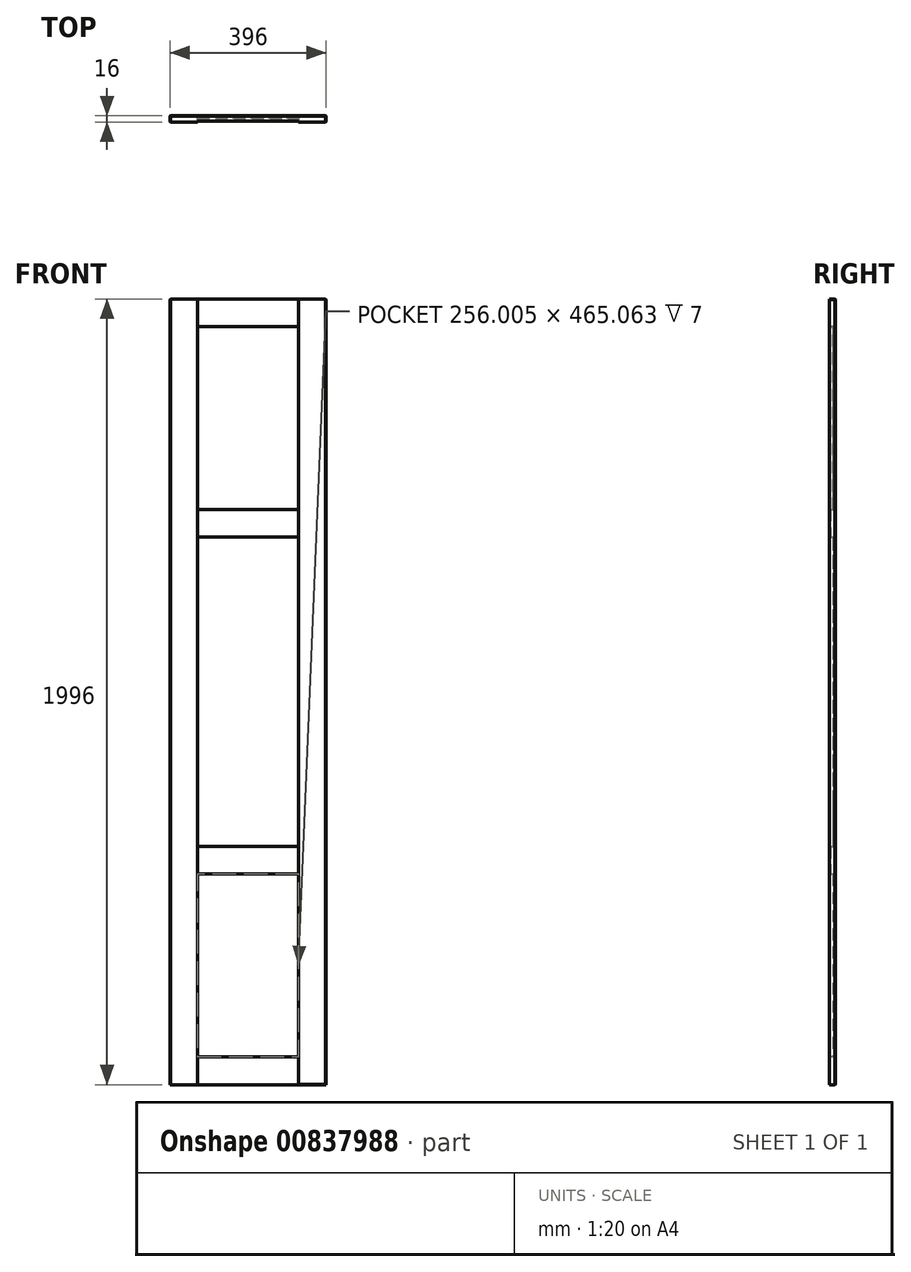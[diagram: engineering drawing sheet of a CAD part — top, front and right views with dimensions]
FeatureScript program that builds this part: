
annotation { "Feature Type Name" : "Feature", "Feature Type Description" : "" }
export const myFeature = defineFeature(function(context is Context, id is Id, definition is map)
    precondition{}
    {
        {
            var Q0;
            Q0=qCreatedBy(makeId("Front.planeOp"),FACE);
            var sketch = newSketch(context, id + "F0", { "sketchPlane" : qUnion([Q0])});
            skLineSegment(sketch, "E0.bottom", {"start": v(0, 0) * mm, "end": v(35.9, 0) * mm});
            skLineSegment(sketch, "E0.top", {"start": v(0, 30.12) * mm, "end": v(35.9, 30.12) * mm});
            skLineSegment(sketch, "E0.left", {"start": v(0, 0) * mm, "end": v(0, 30.12) * mm});
            skLineSegment(sketch, "E0.right", {"start": v(35.9, 0) * mm, "end": v(35.9, 30.12) * mm});
            skSolve(sketch);
        }
        {
            var Q0;
            Q0=makeQuery(id+"F0.imprint","IMPRINT",FACE,{"disambiguationData":[TD([[makeQuery(id+"F0.imprint","IMPRINT",EDGE,{"derivedFrom":sQuery(id+"F0.wireOp",EDGE,"E0.bottom")}),1.0]])]});
            extrude(context, id + "F1", {"entities" : qUnion([Q0]), "depth" : 16 * mm, "offsetDistance" : 25.4 * mm});
        }
        {
            var Q0;
            Q0=makeQuery(id+"F1.opExtrude","SWEPT_FACE",FACE,{"disambiguationData":[OSD([sQuery(id+"F0.wireOp",EDGE,"E0.left")])]});
            extrude(context, id + "F2", {"entities" : qUnion([Q0]), "operationType" : NewBodyOperationType.ADD, "oppositeDirection" : true, "depth" : 196 * mm, "offsetDistance" : 25 * mm});
        }
        {
            var Q0;
            {var subQ0=sQuery(id+"F0.wireOp",EDGE,"E0.bottom");Q0=makeQuery(id+"F2.boolean.opBoolean","MERGE",FACE,{"derivedFrom":[makeQuery(id+"F1.opExtrude","SWEPT_FACE",FACE,{"disambiguationData":[OSD([subQ0])]}),makeQuery(id+"F2.opExtrude","SWEPT_FACE",FACE,{"disambiguationData":[OSD([subQ0,sQuery(id+"F0.wireOp",EDGE,"E0.left")])]})]});}
            extrude(context, id + "F3", {"entities" : qUnion([Q0]), "operationType" : NewBodyOperationType.ADD, "oppositeDirection" : true, "depth" : 796 * mm, "offsetDistance" : 25 * mm});
        }
        {
            var Q0;
            {var subQ0=sQuery(id+"F0.wireOp",EDGE,"E0.left");var subQ1=sQuery(id+"F0.wireOp",EDGE,"E0.bottom");Q0=makeQuery(id+"F3.boolean.opBoolean","MERGE",FACE,{"derivedFrom":[makeQuery(id+"F2.boolean.opBoolean","MERGE",FACE,{"derivedFrom":[makeQuery(id+"F1.opExtrude","CAP_FACE",FACE,{"disambiguationData":[OSD([subQ1,sQuery(id+"F0.wireOp",EDGE,"E0.top"),subQ0,sQuery(id+"F0.wireOp",EDGE,"E0.right")])],"isStart":false}),makeQuery(id+"F2.opExtrude","SWEPT_FACE",FACE,{"disambiguationData":[OSD([subQ0]),TDD([makeQuery(id+"F1.opExtrude","CAP_EDGE",EDGE,{"disambiguationData":[OSD([subQ0])],"isStart":false})])]})]}),makeQuery(id+"F3.opExtrude","SWEPT_FACE",FACE,{"disambiguationData":[OSD([subQ1,subQ0]),TDD([makeQuery(id+"F2.boolean.opBoolean","MERGE",EDGE,{"derivedFrom":[makeQuery(id+"F1.opExtrude","CAP_EDGE",EDGE,{"disambiguationData":[OSD([subQ1])],"isStart":false}),makeQuery(id+"F2.opExtrude","SWEPT_EDGE",EDGE,{"disambiguationData":[OSD([subQ1,subQ0]),TDD([makeQuery(id+"F1.opExtrude","CAP_VERTEX",VERTEX,{"disambiguationData":[OSD([subQ1,subQ0])],"isStart":false})])]})]})])]})]});}
            var sketch = newSketch(context, id + "F4", { "sketchPlane" : qUnion([Q0])});
            skLineSegment(sketch, "E1.bottom", {"start": v(0, 796) * mm, "end": v(42.19, 796) * mm});
            skLineSegment(sketch, "E1.top", {"start": v(0, 751.57) * mm, "end": v(42.19, 751.57) * mm});
            skLineSegment(sketch, "E1.left", {"start": v(0, 796) * mm, "end": v(0, 751.57) * mm});
            skLineSegment(sketch, "E1.right", {"start": v(42.19, 796) * mm, "end": v(42.19, 751.57) * mm});
            skLineSegment(sketch, "E2.bottom", {"start": v(196, 796) * mm, "end": v(153.6, 796) * mm});
            skLineSegment(sketch, "E2.top", {"start": v(196, 746.75) * mm, "end": v(153.6, 746.75) * mm});
            skLineSegment(sketch, "E2.left", {"start": v(196, 796) * mm, "end": v(196, 746.75) * mm});
            skLineSegment(sketch, "E2.right", {"start": v(153.6, 796) * mm, "end": v(153.6, 746.75) * mm});
            skSolve(sketch);
        }
        {
            var Q0;
            Q0=makeQuery(id+"F4.imprint","IMPRINT",FACE,{"disambiguationData":[TD([[makeQuery(id+"F4.imprint","IMPRINT",EDGE,{"derivedFrom":sQuery(id+"F4.wireOp",EDGE,"E1.bottom")}),-1.0]])]});
            var Q1;
            Q1=makeQuery(id+"F4.imprint","IMPRINT",FACE,{"disambiguationData":[TD([[makeQuery(id+"F4.imprint","IMPRINT",EDGE,{"derivedFrom":sQuery(id+"F4.wireOp",EDGE,"E2.bottom")}),-1.0]])]});
            extrude(context, id + "F5", {"entities" : qUnion([Q0, Q1]), "operationType" : NewBodyOperationType.ADD, "depth" : 25 * mm, "offsetDistance" : 25 * mm});
        }
        {
            var Q0;
            {var subQ0=sQuery(id+"F0.wireOp",EDGE,"E0.left");var subQ1=sQuery(id+"F0.wireOp",EDGE,"E0.bottom");Q0=makeQuery(id+"F3.boolean.opBoolean","MERGE",FACE,{"derivedFrom":[makeQuery(id+"F2.boolean.opBoolean","MERGE",FACE,{"derivedFrom":[makeQuery(id+"F1.opExtrude","CAP_FACE",FACE,{"disambiguationData":[OSD([subQ1,sQuery(id+"F0.wireOp",EDGE,"E0.top"),subQ0,sQuery(id+"F0.wireOp",EDGE,"E0.right")])],"isStart":false}),makeQuery(id+"F2.opExtrude","SWEPT_FACE",FACE,{"disambiguationData":[OSD([subQ0]),TDD([makeQuery(id+"F1.opExtrude","CAP_EDGE",EDGE,{"disambiguationData":[OSD([subQ0])],"isStart":false})])]})]}),makeQuery(id+"F3.opExtrude","SWEPT_FACE",FACE,{"disambiguationData":[OSD([subQ1,subQ0]),TDD([makeQuery(id+"F2.boolean.opBoolean","MERGE",EDGE,{"derivedFrom":[makeQuery(id+"F1.opExtrude","CAP_EDGE",EDGE,{"disambiguationData":[OSD([subQ1])],"isStart":false}),makeQuery(id+"F2.opExtrude","SWEPT_EDGE",EDGE,{"disambiguationData":[OSD([subQ1,subQ0]),TDD([makeQuery(id+"F1.opExtrude","CAP_VERTEX",VERTEX,{"disambiguationData":[OSD([subQ1,subQ0])],"isStart":false})])]})]})])]})]});}
            var sketch = newSketch(context, id + "F6", { "sketchPlane" : qUnion([Q0])});
            skLineSegment(sketch, "E3.bottom", {"start": v(196, 0) * mm, "end": v(163.38, 0) * mm});
            skLineSegment(sketch, "E3.top", {"start": v(196, 46.55) * mm, "end": v(163.38, 46.55) * mm});
            skLineSegment(sketch, "E3.left", {"start": v(196, 0) * mm, "end": v(196, 46.55) * mm});
            skLineSegment(sketch, "E3.right", {"start": v(163.38, 0) * mm, "end": v(163.38, 46.55) * mm});
            skLineSegment(sketch, "E4.bottom", {"start": v(0, 0) * mm, "end": v(50.28, 0) * mm});
            skLineSegment(sketch, "E4.top", {"start": v(0, 44.4) * mm, "end": v(50.28, 44.4) * mm});
            skLineSegment(sketch, "E4.left", {"start": v(0, 0) * mm, "end": v(0, 44.4) * mm});
            skLineSegment(sketch, "E4.right", {"start": v(50.28, 0) * mm, "end": v(50.28, 44.4) * mm});
            skSolve(sketch);
        }
        {
            var Q0;
            Q0=makeQuery(id+"F6.imprint","IMPRINT",FACE,{"disambiguationData":[TD([[makeQuery(id+"F6.imprint","IMPRINT",EDGE,{"derivedFrom":sQuery(id+"F6.wireOp",EDGE,"E3.bottom")}),1.0]])]});
            var Q1;
            Q1=makeQuery(id+"F6.imprint","IMPRINT",FACE,{"disambiguationData":[TD([[makeQuery(id+"F6.imprint","IMPRINT",EDGE,{"derivedFrom":sQuery(id+"F6.wireOp",EDGE,"E4.bottom")}),1.0]])]});
            extrude(context, id + "F7", {"entities" : qUnion([Q0, Q1]), "operationType" : NewBodyOperationType.ADD, "depth" : 25 * mm, "offsetDistance" : 25 * mm});
        }
        {
            var Q0;
            Q0=makeQuery(id+"F7.opExtrude","SWEPT_FACE",FACE,{"disambiguationData":[OSD([sQuery(id+"F6.wireOp",EDGE,"E4.right")])]});
            extrude(context, id + "F8", {"entities" : qUnion([Q0]), "operationType" : NewBodyOperationType.ADD, "depth" : 19.72 * mm, "offsetDistance" : 25 * mm});
        }
        {
            var Q0;
            {var subQ0=sQuery(id+"F6.wireOp",EDGE,"E4.top");Q0=makeQuery(id+"F8.boolean.opBoolean","MERGE",FACE,{"derivedFrom":[makeQuery(id+"F7.opExtrude","SWEPT_FACE",FACE,{"disambiguationData":[OSD([subQ0])]}),makeQuery(id+"F8.opExtrude","SWEPT_FACE",FACE,{"disambiguationData":[OSD([subQ0,sQuery(id+"F6.wireOp",EDGE,"E4.right")])]})]});}
            extrude(context, id + "F9", {"entities" : qUnion([Q0]), "operationType" : NewBodyOperationType.ADD, "depth" : 25.6 * mm, "offsetDistance" : 25 * mm});
        }
        {
            var Q0;
            Q0=makeQuery(id+"F7.opExtrude","SWEPT_FACE",FACE,{"disambiguationData":[OSD([sQuery(id+"F6.wireOp",EDGE,"E3.right")])]});
            extrude(context, id + "F10", {"entities" : qUnion([Q0]), "operationType" : NewBodyOperationType.ADD, "depth" : 37.38 * mm, "offsetDistance" : 25 * mm});
        }
        {
            var Q0;
            {var subQ0=sQuery(id+"F6.wireOp",EDGE,"E3.top");Q0=makeQuery(id+"F10.boolean.opBoolean","MERGE",FACE,{"derivedFrom":[makeQuery(id+"F7.opExtrude","SWEPT_FACE",FACE,{"disambiguationData":[OSD([subQ0])]}),makeQuery(id+"F10.opExtrude","SWEPT_FACE",FACE,{"disambiguationData":[OSD([subQ0,sQuery(id+"F6.wireOp",EDGE,"E3.right")])]})]});}
            extrude(context, id + "F11", {"entities" : qUnion([Q0]), "operationType" : NewBodyOperationType.ADD, "depth" : 23.45 * mm, "offsetDistance" : 25 * mm});
        }
        {
            var Q0;
            Q0=makeQuery(id+"F5.opExtrude","SWEPT_FACE",FACE,{"disambiguationData":[OSD([sQuery(id+"F4.wireOp",EDGE,"E1.right")])]});
            extrude(context, id + "F12", {"entities" : qUnion([Q0]), "operationType" : NewBodyOperationType.ADD, "depth" : 27.8 * mm, "offsetDistance" : 25 * mm});
        }
        {
            var Q0;
            {var subQ0=sQuery(id+"F4.wireOp",EDGE,"E1.top");Q0=makeQuery(id+"F12.boolean.opBoolean","MERGE",FACE,{"derivedFrom":[makeQuery(id+"F5.opExtrude","SWEPT_FACE",FACE,{"disambiguationData":[OSD([subQ0])]}),makeQuery(id+"F12.opExtrude","SWEPT_FACE",FACE,{"disambiguationData":[OSD([subQ0,sQuery(id+"F4.wireOp",EDGE,"E1.right")])]})]});}
            extrude(context, id + "F13", {"entities" : qUnion([Q0]), "operationType" : NewBodyOperationType.ADD, "depth" : 25.57 * mm, "offsetDistance" : 25 * mm});
        }
        {
            var Q0;
            Q0=makeQuery(id+"F5.opExtrude","SWEPT_FACE",FACE,{"disambiguationData":[OSD([sQuery(id+"F4.wireOp",EDGE,"E2.top")])]});
            extrude(context, id + "F14", {"entities" : qUnion([Q0]), "operationType" : NewBodyOperationType.ADD, "depth" : 20.75 * mm, "offsetDistance" : 25 * mm});
        }
        {
            var Q0;
            {var subQ0=sQuery(id+"F4.wireOp",EDGE,"E2.right");Q0=makeQuery(id+"F14.boolean.opBoolean","MERGE",FACE,{"derivedFrom":[makeQuery(id+"F5.opExtrude","SWEPT_FACE",FACE,{"disambiguationData":[OSD([subQ0])]}),makeQuery(id+"F14.opExtrude","SWEPT_FACE",FACE,{"disambiguationData":[OSD([sQuery(id+"F4.wireOp",EDGE,"E2.top"),subQ0])]})]});}
            extrude(context, id + "F15", {"entities" : qUnion([Q0]), "operationType" : NewBodyOperationType.ADD, "depth" : 27.6 * mm, "offsetDistance" : 25 * mm});
        }
        {
            var Q0;
            {var subQ0=sQuery(id+"F0.wireOp",EDGE,"E0.left");var subQ1=sQuery(id+"F0.wireOp",EDGE,"E0.bottom");Q0=makeQuery(id+"F3.boolean.opBoolean","MERGE",FACE,{"derivedFrom":[makeQuery(id+"F2.boolean.opBoolean","MERGE",FACE,{"derivedFrom":[makeQuery(id+"F1.opExtrude","CAP_FACE",FACE,{"disambiguationData":[OSD([subQ1,sQuery(id+"F0.wireOp",EDGE,"E0.top"),subQ0,sQuery(id+"F0.wireOp",EDGE,"E0.right")])],"isStart":false}),makeQuery(id+"F2.opExtrude","SWEPT_FACE",FACE,{"disambiguationData":[OSD([subQ0]),TDD([makeQuery(id+"F1.opExtrude","CAP_EDGE",EDGE,{"disambiguationData":[OSD([subQ0])],"isStart":false})])]})]}),makeQuery(id+"F3.opExtrude","SWEPT_FACE",FACE,{"disambiguationData":[OSD([subQ1,subQ0]),TDD([makeQuery(id+"F2.boolean.opBoolean","MERGE",EDGE,{"derivedFrom":[makeQuery(id+"F1.opExtrude","CAP_EDGE",EDGE,{"disambiguationData":[OSD([subQ1])],"isStart":false}),makeQuery(id+"F2.opExtrude","SWEPT_EDGE",EDGE,{"disambiguationData":[OSD([subQ1,subQ0]),TDD([makeQuery(id+"F1.opExtrude","CAP_VERTEX",VERTEX,{"disambiguationData":[OSD([subQ1,subQ0])],"isStart":false})])]})]})])]})]});}
            var sketch = newSketch(context, id + "F16", { "sketchPlane" : qUnion([Q0])});
            skLineSegment(sketch, "E5.bottom", {"start": v(70, 726) * mm, "end": v(126, 726) * mm});
            skLineSegment(sketch, "E5.top", {"start": v(70, 70) * mm, "end": v(126, 70) * mm});
            skLineSegment(sketch, "E5.left", {"start": v(70, 726) * mm, "end": v(70, 70) * mm});
            skLineSegment(sketch, "E5.right", {"start": v(126, 726) * mm, "end": v(126, 70) * mm});
            skSolve(sketch);
        }
        {
            var Q0;
            Q0=makeQuery(id+"F16.imprint","IMPRINT",FACE,{"disambiguationData":[TD([[makeQuery(id+"F16.imprint","IMPRINT",EDGE,{"derivedFrom":sQuery(id+"F16.wireOp",EDGE,"E5.top")}),1.0]])]});
            extrude(context, id + "F17", {"entities" : qUnion([Q0]), "operationType" : NewBodyOperationType.REMOVE, "oppositeDirection" : true, "depth" : 10 * mm, "offsetDistance" : 25 * mm});
        }
        {
            var Q0;
            {var subQ2=sQuery(id+"F0.wireOp",EDGE,"E0.left");var subQ3=sQuery(id+"F0.wireOp",EDGE,"E0.bottom");var subQ4=makeQuery(id+"F1.opExtrude","CAP_FACE",FACE,{"disambiguationData":[OSD([subQ3,sQuery(id+"F0.wireOp",EDGE,"E0.top"),subQ2,sQuery(id+"F0.wireOp",EDGE,"E0.right")])],"isStart":false});var subQ7=makeQuery(id+"F3.opExtrude","SWEPT_FACE",FACE,{"disambiguationData":[OSD([subQ3,subQ2]),TDD([makeQuery(id+"F2.boolean.opBoolean","MERGE",EDGE,{"derivedFrom":[makeQuery(id+"F1.opExtrude","CAP_EDGE",EDGE,{"disambiguationData":[OSD([subQ3])],"isStart":false}),makeQuery(id+"F2.opExtrude","SWEPT_EDGE",EDGE,{"disambiguationData":[OSD([subQ3,subQ2]),TDD([makeQuery(id+"F1.opExtrude","CAP_VERTEX",VERTEX,{"disambiguationData":[OSD([subQ3,subQ2])],"isStart":false})])]})]})])]});var subQ8=makeQuery(id+"F2.opExtrude","SWEPT_FACE",FACE,{"disambiguationData":[OSD([subQ2]),TDD([makeQuery(id+"F1.opExtrude","CAP_EDGE",EDGE,{"disambiguationData":[OSD([subQ2])],"isStart":false})])]});Q0=makeQuery(id+"F17.boolean.opBoolean","SPLIT",FACE,{"disambiguationData":[TD([makeQuery(id+"F1.opExtrude","SWEPT_FACE",FACE,{"disambiguationData":[OSD([subQ3])]})])],"derivedFrom":makeQuery(id+"F3.boolean.opBoolean","MERGE",FACE,{"derivedFrom":[makeQuery(id+"F2.boolean.opBoolean","MERGE",FACE,{"derivedFrom":[subQ4,subQ8]}),subQ7]})});}
            var Q1;
            {var subQ2=sQuery(id+"F4.wireOp",EDGE,"E1.bottom");var subQ3=sQuery(id+"F0.wireOp",EDGE,"E0.left");var subQ4=sQuery(id+"F0.wireOp",EDGE,"E0.bottom");var subQ6=makeQuery(id+"F1.opExtrude","CAP_FACE",FACE,{"disambiguationData":[OSD([subQ4,sQuery(id+"F0.wireOp",EDGE,"E0.top"),subQ3,sQuery(id+"F0.wireOp",EDGE,"E0.right")])],"isStart":false});var subQ7=makeQuery(id+"F2.opExtrude","SWEPT_FACE",FACE,{"disambiguationData":[OSD([subQ3]),TDD([makeQuery(id+"F1.opExtrude","CAP_EDGE",EDGE,{"disambiguationData":[OSD([subQ3])],"isStart":false})])]});var subQ8=makeQuery(id+"F3.opExtrude","SWEPT_FACE",FACE,{"disambiguationData":[OSD([subQ4,subQ3]),TDD([makeQuery(id+"F2.boolean.opBoolean","MERGE",EDGE,{"derivedFrom":[makeQuery(id+"F1.opExtrude","CAP_EDGE",EDGE,{"disambiguationData":[OSD([subQ4])],"isStart":false}),makeQuery(id+"F2.opExtrude","SWEPT_EDGE",EDGE,{"disambiguationData":[OSD([subQ4,subQ3]),TDD([makeQuery(id+"F1.opExtrude","CAP_VERTEX",VERTEX,{"disambiguationData":[OSD([subQ4,subQ3])],"isStart":false})])]})]})])]});Q1=makeQuery(id+"F17.boolean.opBoolean","SPLIT",FACE,{"disambiguationData":[TD([makeQuery(id+"F5.opExtrude","SWEPT_FACE",FACE,{"disambiguationData":[OSD([subQ2])]})])],"derivedFrom":makeQuery(id+"F3.boolean.opBoolean","MERGE",FACE,{"derivedFrom":[makeQuery(id+"F2.boolean.opBoolean","MERGE",FACE,{"derivedFrom":[subQ6,subQ7]}),subQ8]})});}
            extrude(context, id + "F18", {"entities" : qUnion([Q0, Q1]), "operationType" : NewBodyOperationType.REMOVE, "oppositeDirection" : true, "depth" : 2 * mm, "offsetDistance" : 25 * mm});
        }
        {
            var Q0;
            {var subQ0=sQuery(id+"F4.wireOp",EDGE,"E1.right");var subQ1=sQuery(id+"F4.wireOp",EDGE,"E1.top");Q0=makeQuery(id+"F13.boolean.opBoolean","MERGE",FACE,{"derivedFrom":[makeQuery(id+"F12.boolean.opBoolean","MERGE",FACE,{"derivedFrom":[makeQuery(id+"F5.opExtrude","CAP_FACE",FACE,{"disambiguationData":[OSD([sQuery(id+"F4.wireOp",EDGE,"E1.bottom"),subQ1,sQuery(id+"F4.wireOp",EDGE,"E1.left"),subQ0])],"isStart":false}),makeQuery(id+"F12.opExtrude","SWEPT_FACE",FACE,{"disambiguationData":[OSD([subQ0]),TDD([makeQuery(id+"F5.opExtrude","CAP_EDGE",EDGE,{"disambiguationData":[OSD([subQ0])],"isStart":false})])]})]}),makeQuery(id+"F13.opExtrude","SWEPT_FACE",FACE,{"disambiguationData":[OSD([subQ1,subQ0]),TDD([makeQuery(id+"F12.boolean.opBoolean","MERGE",EDGE,{"derivedFrom":[makeQuery(id+"F5.opExtrude","CAP_EDGE",EDGE,{"disambiguationData":[OSD([subQ1])],"isStart":false}),makeQuery(id+"F12.opExtrude","SWEPT_EDGE",EDGE,{"disambiguationData":[OSD([subQ1,subQ0]),TDD([makeQuery(id+"F5.opExtrude","CAP_VERTEX",VERTEX,{"disambiguationData":[OSD([subQ1,subQ0])],"isStart":false})])]})]})])]})]});}
            var Q1;
            {var subQ0=sQuery(id+"F4.wireOp",EDGE,"E2.right");var subQ1=sQuery(id+"F4.wireOp",EDGE,"E2.top");Q1=makeQuery(id+"F15.boolean.opBoolean","MERGE",FACE,{"derivedFrom":[makeQuery(id+"F14.boolean.opBoolean","MERGE",FACE,{"derivedFrom":[makeQuery(id+"F5.opExtrude","CAP_FACE",FACE,{"disambiguationData":[OSD([sQuery(id+"F4.wireOp",EDGE,"E2.bottom"),subQ1,sQuery(id+"F4.wireOp",EDGE,"E2.left"),subQ0])],"isStart":false}),makeQuery(id+"F14.opExtrude","SWEPT_FACE",FACE,{"disambiguationData":[OSD([subQ1]),TDD([makeQuery(id+"F5.opExtrude","CAP_EDGE",EDGE,{"disambiguationData":[OSD([subQ1])],"isStart":false})])]})]}),makeQuery(id+"F15.opExtrude","SWEPT_FACE",FACE,{"disambiguationData":[OSD([subQ1,subQ0]),TDD([makeQuery(id+"F14.boolean.opBoolean","MERGE",EDGE,{"derivedFrom":[makeQuery(id+"F5.opExtrude","CAP_EDGE",EDGE,{"disambiguationData":[OSD([subQ0])],"isStart":false}),makeQuery(id+"F14.opExtrude","SWEPT_EDGE",EDGE,{"disambiguationData":[OSD([subQ1,subQ0]),TDD([makeQuery(id+"F5.opExtrude","CAP_VERTEX",VERTEX,{"disambiguationData":[OSD([subQ1,subQ0])],"isStart":false})])]})]})])]})]});}
            var Q2;
            {var subQ0=sQuery(id+"F6.wireOp",EDGE,"E4.right");var subQ1=sQuery(id+"F6.wireOp",EDGE,"E4.top");Q2=makeQuery(id+"F9.boolean.opBoolean","MERGE",FACE,{"derivedFrom":[makeQuery(id+"F8.boolean.opBoolean","MERGE",FACE,{"derivedFrom":[makeQuery(id+"F7.opExtrude","CAP_FACE",FACE,{"disambiguationData":[OSD([sQuery(id+"F6.wireOp",EDGE,"E4.bottom"),subQ1,sQuery(id+"F6.wireOp",EDGE,"E4.left"),subQ0])],"isStart":false}),makeQuery(id+"F8.opExtrude","SWEPT_FACE",FACE,{"disambiguationData":[OSD([subQ0]),TDD([makeQuery(id+"F7.opExtrude","CAP_EDGE",EDGE,{"disambiguationData":[OSD([subQ0])],"isStart":false})])]})]}),makeQuery(id+"F9.opExtrude","SWEPT_FACE",FACE,{"disambiguationData":[OSD([subQ1,subQ0]),TDD([makeQuery(id+"F8.boolean.opBoolean","MERGE",EDGE,{"derivedFrom":[makeQuery(id+"F7.opExtrude","CAP_EDGE",EDGE,{"disambiguationData":[OSD([subQ1])],"isStart":false}),makeQuery(id+"F8.opExtrude","SWEPT_EDGE",EDGE,{"disambiguationData":[OSD([subQ1,subQ0]),TDD([makeQuery(id+"F7.opExtrude","CAP_VERTEX",VERTEX,{"disambiguationData":[OSD([subQ1,subQ0])],"isStart":false})])]})]})])]})]});}
            var Q3;
            {var subQ0=sQuery(id+"F6.wireOp",EDGE,"E3.right");var subQ1=sQuery(id+"F6.wireOp",EDGE,"E3.top");Q3=makeQuery(id+"F11.boolean.opBoolean","MERGE",FACE,{"derivedFrom":[makeQuery(id+"F10.boolean.opBoolean","MERGE",FACE,{"derivedFrom":[makeQuery(id+"F7.opExtrude","CAP_FACE",FACE,{"disambiguationData":[OSD([sQuery(id+"F6.wireOp",EDGE,"E3.bottom"),subQ1,sQuery(id+"F6.wireOp",EDGE,"E3.left"),subQ0])],"isStart":false}),makeQuery(id+"F10.opExtrude","SWEPT_FACE",FACE,{"disambiguationData":[OSD([subQ0]),TDD([makeQuery(id+"F7.opExtrude","CAP_EDGE",EDGE,{"disambiguationData":[OSD([subQ0])],"isStart":false})])]})]}),makeQuery(id+"F11.opExtrude","SWEPT_FACE",FACE,{"disambiguationData":[OSD([subQ1,subQ0]),TDD([makeQuery(id+"F10.boolean.opBoolean","MERGE",EDGE,{"derivedFrom":[makeQuery(id+"F7.opExtrude","CAP_EDGE",EDGE,{"disambiguationData":[OSD([subQ1])],"isStart":false}),makeQuery(id+"F10.opExtrude","SWEPT_EDGE",EDGE,{"disambiguationData":[OSD([subQ1,subQ0]),TDD([makeQuery(id+"F7.opExtrude","CAP_VERTEX",VERTEX,{"disambiguationData":[OSD([subQ1,subQ0])],"isStart":false})])]})]})])]})]});}
            extrude(context, id + "F19", {"entities" : qUnion([Q0, Q1, Q2, Q3]), "operationType" : NewBodyOperationType.REMOVE, "oppositeDirection" : true, "depth" : 25 * mm, "offsetDistance" : 25 * mm});
        }
        {
            var Q0;
            {var subQ0=sQuery(id+"F4.wireOp",EDGE,"E2.left");var subQ1=sQuery(id+"F0.wireOp",EDGE,"E0.left");var subQ2=sQuery(id+"F0.wireOp",EDGE,"E0.bottom");var subQ3=sQuery(id+"F6.wireOp",EDGE,"E3.left");Q0=makeQuery(id+"F14.boolean.opBoolean","MERGE",FACE,{"derivedFrom":[makeQuery(id+"F11.boolean.opBoolean","MERGE",FACE,{"derivedFrom":[makeQuery(id+"F7.boolean.opBoolean","MERGE",FACE,{"derivedFrom":[makeQuery(id+"F5.boolean.opBoolean","MERGE",FACE,{"derivedFrom":[makeQuery(id+"F3.boolean.opBoolean","MERGE",FACE,{"derivedFrom":[makeQuery(id+"F2.opExtrude","CAP_FACE",FACE,{"disambiguationData":[OSD([subQ1])],"isStart":false}),makeQuery(id+"F3.opExtrude","SWEPT_FACE",FACE,{"disambiguationData":[OSD([subQ2,subQ1]),TDD([makeQuery(id+"F2.opExtrude","CAP_EDGE",EDGE,{"disambiguationData":[OSD([subQ2,subQ1])],"isStart":false})])]})]}),makeQuery(id+"F5.opExtrude","SWEPT_FACE",FACE,{"disambiguationData":[OSD([subQ0])]})]}),makeQuery(id+"F7.opExtrude","SWEPT_FACE",FACE,{"disambiguationData":[OSD([subQ3])]})]}),makeQuery(id+"F11.opExtrude","SWEPT_FACE",FACE,{"disambiguationData":[OSD([subQ2,subQ1,sQuery(id+"F6.wireOp",EDGE,"E3.top"),subQ3])]})]}),makeQuery(id+"F14.opExtrude","SWEPT_FACE",FACE,{"disambiguationData":[OSD([subQ2,subQ1,sQuery(id+"F4.wireOp",EDGE,"E2.top"),subQ0])]})]});}
            extrude(context, id + "F20", {"entities" : qUnion([Q0]), "operationType" : NewBodyOperationType.ADD, "depth" : 200 * mm, "offsetDistance" : 25 * mm});
        }
        {
            var Q0;
            {var subQ0=sQuery(id+"F4.wireOp",EDGE,"E2.right");var subQ1=sQuery(id+"F4.wireOp",EDGE,"E2.top");Q0=makeQuery(id+"F18.boolean.opBoolean","MERGE",FACE,{"derivedFrom":[makeQuery(id+"F15.opExtrude","CAP_FACE",FACE,{"disambiguationData":[OSD([subQ1,subQ0])],"isStart":false}),makeQuery(id+"F18.opExtrude","SWEPT_FACE",FACE,{"disambiguationData":[OSD([subQ1,subQ0])]})]});}
            var Q1;
            {var subQ0=sQuery(id+"F6.wireOp",EDGE,"E3.right");var subQ1=sQuery(id+"F6.wireOp",EDGE,"E3.top");Q1=makeQuery(id+"F18.boolean.opBoolean","MERGE",FACE,{"derivedFrom":[makeQuery(id+"F11.boolean.opBoolean","MERGE",FACE,{"derivedFrom":[makeQuery(id+"F10.opExtrude","CAP_FACE",FACE,{"disambiguationData":[OSD([subQ0])],"isStart":false}),makeQuery(id+"F11.opExtrude","SWEPT_FACE",FACE,{"disambiguationData":[OSD([subQ1,subQ0]),TDD([makeQuery(id+"F10.opExtrude","CAP_EDGE",EDGE,{"disambiguationData":[OSD([subQ1,subQ0])],"isStart":false})])]})]}),makeQuery(id+"F17.boolean.opBoolean","COPY",FACE,{"derivedFrom":makeQuery(id+"F17.opExtrude","SWEPT_FACE",FACE,{"disambiguationData":[OSD([sQuery(id+"F16.wireOp",EDGE,"E5.right")])]})}),makeQuery(id+"F18.opExtrude","SWEPT_FACE",FACE,{"disambiguationData":[OSD([subQ1,subQ0])]})]});}
            extrude(context, id + "F21", {"entities" : qUnion([Q0, Q1]), "operationType" : NewBodyOperationType.REMOVE, "oppositeDirection" : true, "depth" : 200 * mm, "offsetDistance" : 25 * mm});
        }
        {
            var Q0;
            {var subQ0=sQuery(id+"F4.wireOp",EDGE,"E2.bottom");var subQ1=sQuery(id+"F0.wireOp",EDGE,"E0.left");var subQ2=sQuery(id+"F0.wireOp",EDGE,"E0.bottom");var subQ3=sQuery(id+"F4.wireOp",EDGE,"E1.bottom");Q0=makeQuery(id+"F20.boolean.opBoolean","MERGE",FACE,{"derivedFrom":[makeQuery(id+"F15.boolean.opBoolean","MERGE",FACE,{"derivedFrom":[makeQuery(id+"F12.boolean.opBoolean","MERGE",FACE,{"derivedFrom":[makeQuery(id+"F5.boolean.opBoolean","MERGE",FACE,{"derivedFrom":[makeQuery(id+"F3.opExtrude","CAP_FACE",FACE,{"disambiguationData":[OSD([subQ2,subQ1])],"isStart":false}),makeQuery(id+"F5.opExtrude","SWEPT_FACE",FACE,{"disambiguationData":[OSD([subQ3])]}),makeQuery(id+"F5.opExtrude","SWEPT_FACE",FACE,{"disambiguationData":[OSD([subQ0])]})]}),makeQuery(id+"F12.opExtrude","SWEPT_FACE",FACE,{"disambiguationData":[OSD([subQ2,subQ1,subQ3,sQuery(id+"F4.wireOp",EDGE,"E1.right")])]})]}),makeQuery(id+"F15.opExtrude","SWEPT_FACE",FACE,{"disambiguationData":[OSD([subQ2,subQ1,subQ0,sQuery(id+"F4.wireOp",EDGE,"E2.right")])]})]}),makeQuery(id+"F20.opExtrude","SWEPT_FACE",FACE,{"disambiguationData":[OSD([subQ2,subQ1,subQ0,sQuery(id+"F4.wireOp",EDGE,"E2.left")])]})]});}
            extrude(context, id + "F22", {"entities" : qUnion([Q0]), "operationType" : NewBodyOperationType.ADD, "depth" : 200 * mm, "offsetDistance" : 25 * mm});
        }
        {
            var Q0;
            Q0=makeQuery(id+"F17.boolean.opBoolean","COPY",FACE,{"derivedFrom":makeQuery(id+"F17.opExtrude","SWEPT_FACE",FACE,{"disambiguationData":[OSD([sQuery(id+"F16.wireOp",EDGE,"E5.bottom")])]})});
            var Q1;
            {var subQ0=sQuery(id+"F16.wireOp",EDGE,"E5.right");var subQ1=sQuery(id+"F16.wireOp",EDGE,"E5.bottom");var subQ2=sQuery(id+"F4.wireOp",EDGE,"E2.right");var subQ3=sQuery(id+"F4.wireOp",EDGE,"E2.top");var subQ4=makeQuery(id+"F17.boolean.opBoolean","COPY",EDGE,{"derivedFrom":makeQuery(id+"F17.opExtrude","SWEPT_EDGE",EDGE,{"disambiguationData":[OSD([subQ3,subQ2,subQ1,subQ0])]})});Q1=makeQuery(id+"F21.boolean.opBoolean","COPY",FACE,{"derivedFrom":makeQuery(id+"F21.opExtrude","SWEPT_FACE",FACE,{"disambiguationData":[OSD([subQ3,subQ2,subQ1,subQ0]),TDD([makeQuery(id+"F18.boolean.opBoolean","MERGE",EDGE,{"derivedFrom":[subQ4,makeQuery(id+"F18.opExtrude","SWEPT_EDGE",EDGE,{"disambiguationData":[OSD([subQ3,subQ2,subQ1,subQ0])]})]}),makeQuery(id+"F18.boolean.opBoolean","SPLIT",EDGE,{"derivedFrom":subQ4})])]})});}
            extrude(context, id + "F23", {"entities" : qUnion([Q0, Q1]), "operationType" : NewBodyOperationType.REMOVE, "oppositeDirection" : true, "depth" : 200 * mm, "offsetDistance" : 25 * mm});
        }
        {
            var Q0;
            Q0=makeQuery(id+"F22.opExtrude","CAP_FACE",FACE,{"disambiguationData":[OSD([sQuery(id+"F0.wireOp",EDGE,"E0.bottom"),sQuery(id+"F0.wireOp",EDGE,"E0.left"),sQuery(id+"F4.wireOp",EDGE,"E1.bottom"),sQuery(id+"F4.wireOp",EDGE,"E1.right"),sQuery(id+"F4.wireOp",EDGE,"E2.bottom"),sQuery(id+"F4.wireOp",EDGE,"E2.left"),sQuery(id+"F4.wireOp",EDGE,"E2.right")])],"isStart":false});
            extrude(context, id + "F24", {"entities" : qUnion([Q0]), "operationType" : NewBodyOperationType.ADD, "depth" : 1000 * mm, "offsetDistance" : 25 * mm});
        }
        {
            var Q0;
            Q0=makeQuery(id+"F23.boolean.opBoolean","COPY",FACE,{"derivedFrom":makeQuery(id+"F23.opExtrude","CAP_FACE",FACE,{"disambiguationData":[OSD([sQuery(id+"F16.wireOp",EDGE,"E5.bottom")])],"isStart":false})});
            var Q1;
            Q1=makeQuery(id+"F23.boolean.opBoolean","COPY",FACE,{"derivedFrom":makeQuery(id+"F23.opExtrude","CAP_FACE",FACE,{"disambiguationData":[OSD([sQuery(id+"F4.wireOp",EDGE,"E2.top"),sQuery(id+"F4.wireOp",EDGE,"E2.right"),sQuery(id+"F16.wireOp",EDGE,"E5.bottom"),sQuery(id+"F16.wireOp",EDGE,"E5.right")])],"isStart":false})});
            extrude(context, id + "F25", {"entities" : qUnion([Q0, Q1]), "operationType" : NewBodyOperationType.REMOVE, "oppositeDirection" : true, "depth" : 1000 * mm, "offsetDistance" : 25 * mm});
        }
        {
            var Q0;
            {var subQ0=sQuery(id+"F16.wireOp",EDGE,"E5.left");var subQ1=sQuery(id+"F16.wireOp",EDGE,"E5.bottom");var subQ2=sQuery(id+"F4.wireOp",EDGE,"E1.right");var subQ3=sQuery(id+"F4.wireOp",EDGE,"E1.top");var subQ4=sQuery(id+"F4.wireOp",EDGE,"E1.bottom");var subQ5=sQuery(id+"F0.wireOp",EDGE,"E0.left");var subQ6=sQuery(id+"F0.wireOp",EDGE,"E0.bottom");var subQ7=makeQuery(id+"F18.boolean.opBoolean","MERGE",EDGE,{"derivedFrom":[makeQuery(id+"F12.opExtrude","CAP_EDGE",EDGE,{"disambiguationData":[OSD([subQ6,subQ5,subQ4,subQ2])],"isStart":false}),makeQuery(id+"F18.opExtrude","SWEPT_EDGE",EDGE,{"disambiguationData":[OSD([subQ6,subQ5,subQ4,subQ2])]})]});Q0=makeQuery(id+"F25.boolean.opBoolean","MERGE",FACE,{"derivedFrom":[makeQuery(id+"F24.boolean.opBoolean","MERGE",FACE,{"derivedFrom":[makeQuery(id+"F23.boolean.opBoolean","MERGE",FACE,{"derivedFrom":[makeQuery(id+"F22.boolean.opBoolean","MERGE",FACE,{"derivedFrom":[makeQuery(id+"F18.boolean.opBoolean","MERGE",FACE,{"derivedFrom":[makeQuery(id+"F13.boolean.opBoolean","MERGE",FACE,{"derivedFrom":[makeQuery(id+"F12.opExtrude","CAP_FACE",FACE,{"disambiguationData":[OSD([subQ2])],"isStart":false}),makeQuery(id+"F13.opExtrude","SWEPT_FACE",FACE,{"disambiguationData":[OSD([subQ3,subQ2]),TDD([makeQuery(id+"F12.opExtrude","CAP_EDGE",EDGE,{"disambiguationData":[OSD([subQ3,subQ2])],"isStart":false})])]})]}),makeQuery(id+"F17.boolean.opBoolean","COPY",FACE,{"derivedFrom":makeQuery(id+"F17.opExtrude","SWEPT_FACE",FACE,{"disambiguationData":[OSD([subQ0])]})}),makeQuery(id+"F18.opExtrude","SWEPT_FACE",FACE,{"disambiguationData":[OSD([subQ3,subQ2])]})]}),makeQuery(id+"F22.opExtrude","SWEPT_FACE",FACE,{"disambiguationData":[OSD([subQ6,subQ5,subQ4,subQ2]),TDD([subQ7])]})]}),makeQuery(id+"F23.opExtrude","SWEPT_FACE",FACE,{"disambiguationData":[OSD([subQ3,subQ2,subQ1,subQ0])]})]}),makeQuery(id+"F24.opExtrude","SWEPT_FACE",FACE,{"disambiguationData":[OSD([subQ6,subQ5,subQ4,subQ2]),TDD([makeQuery(id+"F22.opExtrude","CAP_EDGE",EDGE,{"disambiguationData":[OSD([subQ6,subQ5,subQ4,subQ2]),TDD([subQ7])],"isStart":false})])]})]}),makeQuery(id+"F25.opExtrude","SWEPT_FACE",FACE,{"disambiguationData":[OSD([subQ3,subQ2,subQ1,subQ0])]})]});}
            var sketch = newSketch(context, id + "F26", { "sketchPlane" : qUnion([Q0])});
            skLineSegment(sketch, "E6.bottom", {"start": v(-16, 70) * mm, "end": v(-6, 70) * mm});
            skLineSegment(sketch, "E6.top", {"start": v(-16, 149.51) * mm, "end": v(-6, 149.51) * mm});
            skLineSegment(sketch, "E6.left", {"start": v(-16, 70) * mm, "end": v(-16, 149.51) * mm});
            skLineSegment(sketch, "E6.right", {"start": v(-6, 70) * mm, "end": v(-6, 149.51) * mm});
            skSolve(sketch);
        }
        {
            var Q0;
            Q0=makeQuery(id+"F26.imprint","IMPRINT",FACE,{"disambiguationData":[TD([[makeQuery(id+"F26.imprint","IMPRINT",EDGE,{"derivedFrom":sQuery(id+"F26.wireOp",EDGE,"E6.top")}),-1.0]])]});
            extrude(context, id + "F27", {"entities" : qUnion([Q0]), "operationType" : NewBodyOperationType.ADD, "depth" : 25 * mm, "offsetDistance" : 25 * mm});
        }
        {
            var Q0;
            Q0=makeQuery(id+"F27.opExtrude","SWEPT_FACE",FACE,{"disambiguationData":[OSD([sQuery(id+"F26.wireOp",EDGE,"E6.top")])]});
            extrude(context, id + "F28", {"entities" : qUnion([Q0]), "operationType" : NewBodyOperationType.ADD, "depth" : 370.48 * mm, "offsetDistance" : 25 * mm});
        }
        {
            var Q0;
            {var subQ0=sQuery(id+"F16.wireOp",EDGE,"E5.right");var subQ1=sQuery(id+"F16.wireOp",EDGE,"E5.bottom");var subQ2=sQuery(id+"F4.wireOp",EDGE,"E2.right");var subQ3=sQuery(id+"F4.wireOp",EDGE,"E2.top");var subQ4=makeQuery(id+"F21.boolean.opBoolean","COPY",EDGE,{"derivedFrom":makeQuery(id+"F21.opExtrude","SWEPT_EDGE",EDGE,{"disambiguationData":[OSD([subQ3,subQ2,subQ1,subQ0]),TDD([makeQuery(id+"F17.boolean.opBoolean","COPY",VERTEX,{"derivedFrom":makeQuery(id+"F17.opExtrude","CAP_VERTEX",VERTEX,{"disambiguationData":[OSD([subQ3,subQ2,subQ1,subQ0])],"isStart":false})})])]})});var subQ5=makeQuery(id+"F17.boolean.opBoolean","COPY",EDGE,{"derivedFrom":makeQuery(id+"F17.opExtrude","CAP_EDGE",EDGE,{"disambiguationData":[OSD([subQ1])],"isStart":false})});Q0=makeQuery(id+"F25.boolean.opBoolean","MERGE",FACE,{"derivedFrom":[makeQuery(id+"F23.boolean.opBoolean","MERGE",FACE,{"derivedFrom":[makeQuery(id+"F21.boolean.opBoolean","MERGE",FACE,{"derivedFrom":[makeQuery(id+"F17.boolean.opBoolean","COPY",FACE,{"derivedFrom":makeQuery(id+"F17.opExtrude","CAP_FACE",FACE,{"disambiguationData":[OSD([subQ1,sQuery(id+"F16.wireOp",EDGE,"E5.top"),sQuery(id+"F16.wireOp",EDGE,"E5.left"),subQ0])],"isStart":false})}),makeQuery(id+"F21.opExtrude","SWEPT_FACE",FACE,{"disambiguationData":[OSD([subQ0])]})]}),makeQuery(id+"F23.opExtrude","SWEPT_FACE",FACE,{"disambiguationData":[OSD([subQ1]),TDD([subQ5])]}),makeQuery(id+"F23.opExtrude","SWEPT_FACE",FACE,{"disambiguationData":[OSD([subQ3,subQ2,subQ1,subQ0]),TDD([subQ4])]})]}),makeQuery(id+"F25.opExtrude","SWEPT_FACE",FACE,{"disambiguationData":[OSD([subQ1]),TDD([makeQuery(id+"F23.boolean.opBoolean","COPY",EDGE,{"derivedFrom":makeQuery(id+"F23.opExtrude","CAP_EDGE",EDGE,{"disambiguationData":[OSD([subQ1]),TDD([subQ5])],"isStart":false})})])]}),makeQuery(id+"F25.opExtrude","SWEPT_FACE",FACE,{"disambiguationData":[OSD([subQ3,subQ2,subQ1,subQ0]),TDD([makeQuery(id+"F23.boolean.opBoolean","COPY",EDGE,{"derivedFrom":makeQuery(id+"F23.opExtrude","CAP_EDGE",EDGE,{"disambiguationData":[OSD([subQ3,subQ2,subQ1,subQ0]),TDD([subQ4])],"isStart":false})})])]})]});}
            var sketch = newSketch(context, id + "F29", { "sketchPlane" : qUnion([Q0])});
            skLineSegment(sketch, "E7.bottom", {"start": v(70, 535.07) * mm, "end": v(326, 535.07) * mm});
            skLineSegment(sketch, "E7.top", {"start": v(70, 621.83) * mm, "end": v(326, 621.83) * mm});
            skLineSegment(sketch, "E7.left", {"start": v(70, 535.07) * mm, "end": v(70, 621.83) * mm});
            skLineSegment(sketch, "E7.right", {"start": v(326, 535.07) * mm, "end": v(326, 621.83) * mm});
            skSolve(sketch);
        }
        {
            var Q0;
            Q0=makeQuery(id+"F29.imprint","IMPRINT",FACE,{"disambiguationData":[TD([[makeQuery(id+"F29.imprint","IMPRINT",EDGE,{"derivedFrom":sQuery(id+"F29.wireOp",EDGE,"E7.bottom")}),1.0]])]});
            extrude(context, id + "F30", {"entities" : qUnion([Q0]), "operationType" : NewBodyOperationType.ADD, "depth" : 7 * mm, "offsetDistance" : 25 * mm});
        }
        {
            var Q0;
            {var subQ0=sQuery(id+"F26.wireOp",EDGE,"E6.top");Q0=makeQuery(id+"F28.boolean.opBoolean","MERGE",FACE,{"derivedFrom":[makeQuery(id+"F27.opExtrude","CAP_FACE",FACE,{"disambiguationData":[OSD([sQuery(id+"F26.wireOp",EDGE,"E6.bottom"),subQ0,sQuery(id+"F26.wireOp",EDGE,"E6.left"),sQuery(id+"F26.wireOp",EDGE,"E6.right")])],"isStart":false}),makeQuery(id+"F28.opExtrude","SWEPT_FACE",FACE,{"disambiguationData":[OSD([subQ0]),TDD([makeQuery(id+"F27.opExtrude","CAP_EDGE",EDGE,{"disambiguationData":[OSD([subQ0])],"isStart":false})])]})]});}
            extrude(context, id + "F31", {"entities" : qUnion([Q0]), "operationType" : NewBodyOperationType.REMOVE, "oppositeDirection" : true, "depth" : 25 * mm, "offsetDistance" : 25 * mm});
        }
        {
            var Q0;
            {var subQ0=sQuery(id+"F16.wireOp",EDGE,"E5.left");var subQ1=sQuery(id+"F16.wireOp",EDGE,"E5.bottom");var subQ2=sQuery(id+"F4.wireOp",EDGE,"E1.right");var subQ3=sQuery(id+"F4.wireOp",EDGE,"E1.top");var subQ4=sQuery(id+"F4.wireOp",EDGE,"E1.bottom");var subQ5=sQuery(id+"F0.wireOp",EDGE,"E0.left");var subQ6=sQuery(id+"F0.wireOp",EDGE,"E0.bottom");var subQ7=makeQuery(id+"F18.boolean.opBoolean","MERGE",EDGE,{"derivedFrom":[makeQuery(id+"F12.opExtrude","CAP_EDGE",EDGE,{"disambiguationData":[OSD([subQ6,subQ5,subQ4,subQ2])],"isStart":false}),makeQuery(id+"F18.opExtrude","SWEPT_EDGE",EDGE,{"disambiguationData":[OSD([subQ6,subQ5,subQ4,subQ2])]})]});Q0=makeQuery(id+"F31.boolean.opBoolean","MERGE",FACE,{"derivedFrom":[makeQuery(id+"F25.boolean.opBoolean","MERGE",FACE,{"derivedFrom":[makeQuery(id+"F24.boolean.opBoolean","MERGE",FACE,{"derivedFrom":[makeQuery(id+"F23.boolean.opBoolean","MERGE",FACE,{"derivedFrom":[makeQuery(id+"F22.boolean.opBoolean","MERGE",FACE,{"derivedFrom":[makeQuery(id+"F18.boolean.opBoolean","MERGE",FACE,{"derivedFrom":[makeQuery(id+"F13.boolean.opBoolean","MERGE",FACE,{"derivedFrom":[makeQuery(id+"F12.opExtrude","CAP_FACE",FACE,{"disambiguationData":[OSD([subQ2])],"isStart":false}),makeQuery(id+"F13.opExtrude","SWEPT_FACE",FACE,{"disambiguationData":[OSD([subQ3,subQ2]),TDD([makeQuery(id+"F12.opExtrude","CAP_EDGE",EDGE,{"disambiguationData":[OSD([subQ3,subQ2])],"isStart":false})])]})]}),makeQuery(id+"F17.boolean.opBoolean","COPY",FACE,{"derivedFrom":makeQuery(id+"F17.opExtrude","SWEPT_FACE",FACE,{"disambiguationData":[OSD([subQ0])]})}),makeQuery(id+"F18.opExtrude","SWEPT_FACE",FACE,{"disambiguationData":[OSD([subQ3,subQ2])]})]}),makeQuery(id+"F22.opExtrude","SWEPT_FACE",FACE,{"disambiguationData":[OSD([subQ6,subQ5,subQ4,subQ2]),TDD([subQ7])]})]}),makeQuery(id+"F23.opExtrude","SWEPT_FACE",FACE,{"disambiguationData":[OSD([subQ3,subQ2,subQ1,subQ0])]})]}),makeQuery(id+"F24.opExtrude","SWEPT_FACE",FACE,{"disambiguationData":[OSD([subQ6,subQ5,subQ4,subQ2]),TDD([makeQuery(id+"F22.opExtrude","CAP_EDGE",EDGE,{"disambiguationData":[OSD([subQ6,subQ5,subQ4,subQ2]),TDD([subQ7])],"isStart":false})])]})]}),makeQuery(id+"F25.opExtrude","SWEPT_FACE",FACE,{"disambiguationData":[OSD([subQ3,subQ2,subQ1,subQ0])]})]}),makeQuery(id+"F31.opExtrude","CAP_FACE",FACE,{"disambiguationData":[OSD([sQuery(id+"F26.wireOp",EDGE,"E6.bottom"),sQuery(id+"F26.wireOp",EDGE,"E6.top"),sQuery(id+"F26.wireOp",EDGE,"E6.left"),sQuery(id+"F26.wireOp",EDGE,"E6.right")])],"isStart":false})]});}
            var sketch = newSketch(context, id + "F32", { "sketchPlane" : qUnion([Q0])});
            skLineSegment(sketch, "E8.bottom", {"start": v(-6, 1926) * mm, "end": v(-16, 1926) * mm});
            skLineSegment(sketch, "E8.top", {"start": v(-6, 1896.17) * mm, "end": v(-16, 1896.17) * mm});
            skLineSegment(sketch, "E8.left", {"start": v(-6, 1926) * mm, "end": v(-6, 1896.17) * mm});
            skLineSegment(sketch, "E8.right", {"start": v(-16, 1926) * mm, "end": v(-16, 1896.17) * mm});
            skSolve(sketch);
        }
        {
            var Q0;
            Q0=makeQuery(id+"F32.imprint","IMPRINT",FACE,{"disambiguationData":[TD([[makeQuery(id+"F32.imprint","IMPRINT",EDGE,{"derivedFrom":sQuery(id+"F32.wireOp",EDGE,"E8.top")}),-1.0]])]});
            extrude(context, id + "F33", {"entities" : qUnion([Q0]), "operationType" : NewBodyOperationType.ADD, "depth" : 25 * mm, "offsetDistance" : 25 * mm});
        }
        {
            var Q0;
            Q0=makeQuery(id+"F33.opExtrude","SWEPT_FACE",FACE,{"disambiguationData":[OSD([sQuery(id+"F32.wireOp",EDGE,"E8.top")])]});
            extrude(context, id + "F34", {"entities" : qUnion([Q0]), "operationType" : NewBodyOperationType.ADD, "depth" : 420.17 * mm, "offsetDistance" : 25 * mm});
        }
        {
            var Q0;
            {var subQ5=sQuery(id+"F16.wireOp",EDGE,"E5.left");var subQ6=sQuery(id+"F16.wireOp",EDGE,"E5.bottom");var subQ8=sQuery(id+"F16.wireOp",EDGE,"E5.right");var subQ9=sQuery(id+"F4.wireOp",EDGE,"E2.right");var subQ10=sQuery(id+"F4.wireOp",EDGE,"E2.top");var subQ13=makeQuery(id+"F21.boolean.opBoolean","COPY",EDGE,{"derivedFrom":makeQuery(id+"F21.opExtrude","SWEPT_EDGE",EDGE,{"disambiguationData":[OSD([subQ10,subQ9,subQ6,subQ8]),TDD([makeQuery(id+"F17.boolean.opBoolean","COPY",VERTEX,{"derivedFrom":makeQuery(id+"F17.opExtrude","CAP_VERTEX",VERTEX,{"disambiguationData":[OSD([subQ10,subQ9,subQ6,subQ8])],"isStart":false})})])]})});var subQ14=makeQuery(id+"F17.boolean.opBoolean","COPY",EDGE,{"derivedFrom":makeQuery(id+"F17.opExtrude","CAP_EDGE",EDGE,{"disambiguationData":[OSD([subQ6])],"isStart":false})});Q0=makeQuery(id+"F30.boolean.opBoolean","SPLIT",FACE,{"disambiguationData":[TD([makeQuery(id+"F25.boolean.opBoolean","COPY",FACE,{"derivedFrom":makeQuery(id+"F25.opExtrude","CAP_FACE",FACE,{"disambiguationData":[OSD([subQ6])],"isStart":false})})])],"derivedFrom":makeQuery(id+"F25.boolean.opBoolean","MERGE",FACE,{"derivedFrom":[makeQuery(id+"F23.boolean.opBoolean","MERGE",FACE,{"derivedFrom":[makeQuery(id+"F21.boolean.opBoolean","MERGE",FACE,{"derivedFrom":[makeQuery(id+"F17.boolean.opBoolean","COPY",FACE,{"derivedFrom":makeQuery(id+"F17.opExtrude","CAP_FACE",FACE,{"disambiguationData":[OSD([subQ6,sQuery(id+"F16.wireOp",EDGE,"E5.top"),subQ5,subQ8])],"isStart":false})}),makeQuery(id+"F21.opExtrude","SWEPT_FACE",FACE,{"disambiguationData":[OSD([subQ8])]})]}),makeQuery(id+"F23.opExtrude","SWEPT_FACE",FACE,{"disambiguationData":[OSD([subQ6]),TDD([subQ14])]}),makeQuery(id+"F23.opExtrude","SWEPT_FACE",FACE,{"disambiguationData":[OSD([subQ10,subQ9,subQ6,subQ8]),TDD([subQ13])]})]}),makeQuery(id+"F25.opExtrude","SWEPT_FACE",FACE,{"disambiguationData":[OSD([subQ6]),TDD([makeQuery(id+"F23.boolean.opBoolean","COPY",EDGE,{"derivedFrom":makeQuery(id+"F23.opExtrude","CAP_EDGE",EDGE,{"disambiguationData":[OSD([subQ6]),TDD([subQ14])],"isStart":false})})])]}),makeQuery(id+"F25.opExtrude","SWEPT_FACE",FACE,{"disambiguationData":[OSD([subQ10,subQ9,subQ6,subQ8]),TDD([makeQuery(id+"F23.boolean.opBoolean","COPY",EDGE,{"derivedFrom":makeQuery(id+"F23.opExtrude","CAP_EDGE",EDGE,{"disambiguationData":[OSD([subQ10,subQ9,subQ6,subQ8]),TDD([subQ13])],"isStart":false})})])]})]})});}
            var sketch = newSketch(context, id + "F35", { "sketchPlane" : qUnion([Q0])});
            skLineSegment(sketch, "E9.bottom", {"start": v(70, 1461.48) * mm, "end": v(326, 1461.48) * mm});
            skLineSegment(sketch, "E9.top", {"start": v(70, 1386.54) * mm, "end": v(326, 1386.54) * mm});
            skLineSegment(sketch, "E9.left", {"start": v(70, 1461.48) * mm, "end": v(70, 1386.54) * mm});
            skLineSegment(sketch, "E9.right", {"start": v(326, 1461.48) * mm, "end": v(326, 1386.54) * mm});
            skSolve(sketch);
        }
        {
            var Q0;
            Q0=makeQuery(id+"F35.imprint","IMPRINT",FACE,{"disambiguationData":[TD([[makeQuery(id+"F35.imprint","IMPRINT",EDGE,{"derivedFrom":sQuery(id+"F35.wireOp",EDGE,"E9.bottom")}),-1.0]])]});
            extrude(context, id + "F36", {"entities" : qUnion([Q0]), "operationType" : NewBodyOperationType.ADD, "depth" : 7 * mm, "offsetDistance" : 25 * mm});
        }
        {
            var Q0;
            {var subQ0=sQuery(id+"F32.wireOp",EDGE,"E8.top");Q0=makeQuery(id+"F34.boolean.opBoolean","MERGE",FACE,{"derivedFrom":[makeQuery(id+"F33.opExtrude","CAP_FACE",FACE,{"disambiguationData":[OSD([sQuery(id+"F32.wireOp",EDGE,"E8.bottom"),subQ0,sQuery(id+"F32.wireOp",EDGE,"E8.left"),sQuery(id+"F32.wireOp",EDGE,"E8.right")])],"isStart":false}),makeQuery(id+"F34.opExtrude","SWEPT_FACE",FACE,{"disambiguationData":[OSD([subQ0]),TDD([makeQuery(id+"F33.opExtrude","CAP_EDGE",EDGE,{"disambiguationData":[OSD([subQ0])],"isStart":false})])]})]});}
            extrude(context, id + "F37", {"entities" : qUnion([Q0]), "operationType" : NewBodyOperationType.REMOVE, "oppositeDirection" : true, "depth" : 25 * mm, "offsetDistance" : 25 * mm});
        }
        {
            var Q0;
            Q0=makeQuery(id+"F36.opExtrude","SWEPT_FACE",FACE,{"disambiguationData":[OSD([sQuery(id+"F35.wireOp",EDGE,"E9.top")])]});
            extrude(context, id + "F38", {"entities" : qUnion([Q0]), "operationType" : NewBodyOperationType.REMOVE, "oppositeDirection" : true, "depth" : 4.93 * mm, "offsetDistance" : 25 * mm});
        }
        {
            var Q0;
            Q0=makeQuery(id+"F30.opExtrude","SWEPT_FACE",FACE,{"disambiguationData":[OSD([sQuery(id+"F29.wireOp",EDGE,"E7.top")])]});
            extrude(context, id + "F39", {"entities" : qUnion([Q0]), "operationType" : NewBodyOperationType.REMOVE, "oppositeDirection" : true, "depth" : 16.76 * mm, "offsetDistance" : 25 * mm});
        }
        {
            var Q0;
            Q0=makeQuery(id+"F24.opExtrude","CAP_EDGE",EDGE,{"disambiguationData":[OSD([sQuery(id+"F0.wireOp",EDGE,"E0.bottom"),sQuery(id+"F0.wireOp",EDGE,"E0.left"),sQuery(id+"F4.wireOp",EDGE,"E2.bottom"),sQuery(id+"F4.wireOp",EDGE,"E2.left"),sQuery(id+"F4.wireOp",EDGE,"E2.right")])],"isStart":false});
            var Q1;
            {var subQ0=sQuery(id+"F4.wireOp",EDGE,"E2.left");var subQ1=sQuery(id+"F4.wireOp",EDGE,"E2.bottom");Q1=makeQuery(id+"F24.boolean.opBoolean","MERGE",EDGE,{"derivedFrom":[makeQuery(id+"F22.boolean.opBoolean","MERGE",EDGE,{"derivedFrom":[makeQuery(id+"F20.opExtrude","CAP_EDGE",EDGE,{"disambiguationData":[OSD([sQuery(id+"F0.wireOp",EDGE,"E0.bottom"),sQuery(id+"F0.wireOp",EDGE,"E0.left"),sQuery(id+"F4.wireOp",EDGE,"E2.top"),subQ0,sQuery(id+"F6.wireOp",EDGE,"E3.top"),sQuery(id+"F6.wireOp",EDGE,"E3.left")])],"isStart":false}),makeQuery(id+"F22.opExtrude","SWEPT_EDGE",EDGE,{"disambiguationData":[OSD([subQ1,subQ0])]})]}),makeQuery(id+"F24.opExtrude","SWEPT_EDGE",EDGE,{"disambiguationData":[OSD([subQ1,subQ0])]})]});}
            var Q2;
            {var subQ0=sQuery(id+"F4.wireOp",EDGE,"E1.right");var subQ1=sQuery(id+"F4.wireOp",EDGE,"E1.bottom");var subQ2=sQuery(id+"F0.wireOp",EDGE,"E0.left");var subQ3=sQuery(id+"F0.wireOp",EDGE,"E0.bottom");Q2=makeQuery(id+"F24.opExtrude","CAP_EDGE",EDGE,{"disambiguationData":[OSD([subQ3,subQ2,subQ1,subQ0]),TDD([makeQuery(id+"F22.opExtrude","CAP_EDGE",EDGE,{"disambiguationData":[OSD([subQ3,subQ2,subQ1,subQ0]),TDD([makeQuery(id+"F19.boolean.opBoolean","COPY",EDGE,{"derivedFrom":makeQuery(id+"F19.opExtrude","CAP_EDGE",EDGE,{"disambiguationData":[OSD([subQ3,subQ2,subQ1,subQ0])],"isStart":false})})])],"isStart":false})])],"isStart":false});}
            var Q3;
            {var subQ0=sQuery(id+"F4.wireOp",EDGE,"E1.left");var subQ1=sQuery(id+"F4.wireOp",EDGE,"E1.bottom");var subQ2=sQuery(id+"F0.wireOp",EDGE,"E0.left");var subQ3=sQuery(id+"F0.wireOp",EDGE,"E0.bottom");Q3=makeQuery(id+"F24.boolean.opBoolean","MERGE",EDGE,{"derivedFrom":[makeQuery(id+"F22.boolean.opBoolean","MERGE",EDGE,{"derivedFrom":[makeQuery(id+"F19.boolean.opBoolean","MERGE",EDGE,{"derivedFrom":[makeQuery(id+"F3.boolean.opBoolean","MERGE",EDGE,{"derivedFrom":[makeQuery(id+"F1.opExtrude","CAP_EDGE",EDGE,{"disambiguationData":[OSD([subQ2])],"isStart":false}),makeQuery(id+"F3.opExtrude","SWEPT_EDGE",EDGE,{"disambiguationData":[OSD([subQ3,subQ2]),TDD([makeQuery(id+"F1.opExtrude","CAP_VERTEX",VERTEX,{"disambiguationData":[OSD([subQ3,subQ2])],"isStart":false})])]})]}),makeQuery(id+"F19.opExtrude","CAP_EDGE",EDGE,{"disambiguationData":[OSD([subQ3,subQ2,sQuery(id+"F6.wireOp",EDGE,"E4.top"),sQuery(id+"F6.wireOp",EDGE,"E4.left")])],"isStart":false}),makeQuery(id+"F19.opExtrude","CAP_EDGE",EDGE,{"disambiguationData":[OSD([subQ3,subQ2,sQuery(id+"F4.wireOp",EDGE,"E1.top"),subQ0])],"isStart":false})]}),makeQuery(id+"F22.opExtrude","SWEPT_EDGE",EDGE,{"disambiguationData":[OSD([subQ1,subQ0])]})]}),makeQuery(id+"F24.opExtrude","SWEPT_EDGE",EDGE,{"disambiguationData":[OSD([subQ1,subQ0])]})]});}
            var Q4;
            Q4=makeQuery(id+"F19.boolean.opBoolean","COPY",EDGE,{"derivedFrom":makeQuery(id+"F19.opExtrude","CAP_EDGE",EDGE,{"disambiguationData":[OSD([sQuery(id+"F0.wireOp",EDGE,"E0.bottom"),sQuery(id+"F0.wireOp",EDGE,"E0.left"),sQuery(id+"F6.wireOp",EDGE,"E4.bottom"),sQuery(id+"F6.wireOp",EDGE,"E4.right")])],"isStart":false})});
            var Q5;
            {var subQ0=sQuery(id+"F6.wireOp",EDGE,"E3.bottom");Q5=makeQuery(id+"F20.boolean.opBoolean","MERGE",EDGE,{"derivedFrom":[makeQuery(id+"F19.boolean.opBoolean","COPY",EDGE,{"derivedFrom":makeQuery(id+"F19.opExtrude","CAP_EDGE",EDGE,{"disambiguationData":[OSD([sQuery(id+"F0.wireOp",EDGE,"E0.bottom"),sQuery(id+"F0.wireOp",EDGE,"E0.left"),subQ0,sQuery(id+"F6.wireOp",EDGE,"E3.right")])],"isStart":false})}),makeQuery(id+"F20.opExtrude","SWEPT_EDGE",EDGE,{"disambiguationData":[OSD([subQ0,sQuery(id+"F6.wireOp",EDGE,"E3.left")])]})]});}
            var Q6;
            {var subQ0=sQuery(id+"F0.wireOp",EDGE,"E0.left");var subQ1=sQuery(id+"F0.wireOp",EDGE,"E0.bottom");Q6=makeQuery(id+"F24.boolean.opBoolean","MERGE",FACE,{"derivedFrom":[makeQuery(id+"F22.boolean.opBoolean","MERGE",FACE,{"derivedFrom":[makeQuery(id+"F20.boolean.opBoolean","MERGE",FACE,{"derivedFrom":[makeQuery(id+"F3.boolean.opBoolean","MERGE",FACE,{"derivedFrom":[makeQuery(id+"F2.boolean.opBoolean","MERGE",FACE,{"derivedFrom":[makeQuery(id+"F1.opExtrude","CAP_FACE",FACE,{"disambiguationData":[OSD([subQ1,sQuery(id+"F0.wireOp",EDGE,"E0.top"),subQ0,sQuery(id+"F0.wireOp",EDGE,"E0.right")])],"isStart":true}),makeQuery(id+"F2.opExtrude","SWEPT_FACE",FACE,{"disambiguationData":[OSD([subQ0]),TDD([makeQuery(id+"F1.opExtrude","CAP_EDGE",EDGE,{"disambiguationData":[OSD([subQ0])],"isStart":true})])]})]}),makeQuery(id+"F3.opExtrude","SWEPT_FACE",FACE,{"disambiguationData":[OSD([subQ1,subQ0]),TDD([makeQuery(id+"F2.boolean.opBoolean","MERGE",EDGE,{"derivedFrom":[makeQuery(id+"F1.opExtrude","CAP_EDGE",EDGE,{"disambiguationData":[OSD([subQ1])],"isStart":true}),makeQuery(id+"F2.opExtrude","SWEPT_EDGE",EDGE,{"disambiguationData":[OSD([subQ1,subQ0]),TDD([makeQuery(id+"F1.opExtrude","CAP_VERTEX",VERTEX,{"disambiguationData":[OSD([subQ1,subQ0])],"isStart":true})])]})]})])]})]}),makeQuery(id+"F20.opExtrude","SWEPT_FACE",FACE,{"disambiguationData":[OSD([subQ1,subQ0])]})]}),makeQuery(id+"F22.opExtrude","SWEPT_FACE",FACE,{"disambiguationData":[OSD([subQ1,subQ0])]})]}),makeQuery(id+"F24.opExtrude","SWEPT_FACE",FACE,{"disambiguationData":[OSD([subQ1,subQ0])]})]});}
            chamfer(context, id + "F40", {"entities" : qUnion([Q0, Q1, Q2, Q3, Q4, Q5, Q6]), "width" : 1 * mm, "tangentPropagation" : true});
        }
    });
